# Revit family: LAMP_HANCE 48V 1000-2000 SPOT DALI
name_source: partatom
category: Luminarias
revit_build: Autodesk Revit 2015 (Build: 20140606_1530(x64)
units: mm (PartAtom-declared; Revit-internal decimal feet)

## types (12) — shared parameters
CRI = 80
Comentarios de tipo = Availability of tilting between 0º and 90º, rotation between 0º and 355º and change ring color when placed in a project.
Diameter = 65 mm  [stored 0.213255 ft]
Elevación por defecto = 1219 mm
Fabricante = LAMP
Gear = Adjustable DALI
Height = 135 mm  [stored 0.442913 ft]
IEE = A+
Installation instructions = https://www.lamp.es
Insulation class = III
Lamp = COB LED
Last update = 02/04/2019
Luminaire type = Indoor - Spotlight
MacAdam = 3
Manufacturer URL = http://www.lamp.es
Manufacturer country = Spain
Manufacturer name = LAMP
Model explanation = Availability of tilting between 0º and 90º, rotation between 0º and 355º and change ring color when placed in a project.
Power Supply = 48V DC
Product URL = https://www.lamp.es
Product datasheet = http://www.lamp.es
Protection rating = IP20
Type = COB PHILIPS
Weight = 0.44 kg

## per-type parameters (varying)
| type | Descripción | Efficacy | Finish | Initial color | Initial intensity | LED Lifetime | Material tija | Modelo | Photometric web file | Plum | Power | Product code |
| 657LM 2700 SPOT BLACK | HANCE TRACK 48 1000 VWW SP DALI BK. | 70 lm/W | RAL9011 textured | 2700 K | 657 lm | 50.000 L90 B10 | LAMP_Aluminio Hance Negro | HS1TL10SP827DBB | Cuerpo Hance 48V BASE 1000_2000 (tilting)_SP : 657LM 2700 SPOT BLACK | 9 W | 9 W | HS1TL10SP827DBB |
| 657LM 2700 SPOT WHITE | HANCE TRACK 48 1000 VWW SP DALI WH. | 70 lm/W | RAL9010 textured | 2700 K | 657 lm | 50.000 L90 B10 | LAMP_Aluminio Hance Blanco | HS1TL10SP827DBW | Cuerpo Hance 48V BASE 1000_2000 (tilting)_SP : 657LM 2700 SPOT WHITE | 9 W | 9 W | HS1TL10SP827DBW |
| 670LM 3000 SPOT BLACK | HANCE TRACK 48 1000 WW SP DALI BK. | 71 lm/W | RAL9011 textured | 3000 K | 670 lm | 50.000 L90 B10 | LAMP_Aluminio Hance Negro | HS1TL10SP830DBB | Cuerpo Hance 48V BASE 1000_2000 (tilting)_SP : 670LM 3000 SPOT BLACK | 9 W | 9 W | HS1TL10SP830DBB |
| 670LM 3000 SPOT WHITE | HANCE TRACK 48 1000 WW SP DALI WH. | 71 lm/W | RAL9010 textured | 3000 K | 670 lm | 50.000 L90 B10 | LAMP_Aluminio Hance Negro | HS1TL10SP830DBW | Cuerpo Hance 48V BASE 1000_2000 (tilting)_SP : 670LM 3000 SPOT WHITE | 9 W | 9 W | HS1TL10SP830DBW |
| 710LM 4000 SPOT BLACK | HANCE TRACK 48 1000 NW SP DALI BK. | 76 lm/W | RAL9011 textured | 4000 K | 710 lm | 50.000 L90 B10 | LAMP_Aluminio Hance Negro | HS1TL10SP840DBB | Cuerpo Hance 48V BASE 1000_2000 (tilting)_SP : 710LM 4000 SPOT BLACK | 9 W | 9 W | HS1TL10SP840DBB |
| 710LM 4000 SPOT WHITE | HANCE TRACK 48 1000 NW SP DALI WH. | 76 lm/W | RAL9010 textured | 4000 K | 710 lm | 50.000 L90 B10 | LAMP_Aluminio Hance Blanco | HS1TL10SP840DBW | Cuerpo Hance 48V BASE 1000_2000 (tilting)_SP : 710LM 4000 SPOT WHITE | 9 W | 9 W | HS1TL10SP840DBW |
| 1427LM 2700 SPOT BLACK | HANCE TRACK 48 2000 VWW SP DALI BK. | 84 lm/W | RAL9011 textured | 2700 K | 1427 lm | 50.000 L80 B10 | LAMP_Aluminio Hance Negro | HS1TL20SP827DBB | Cuerpo Hance 48V BASE 1000_2000 (tilting)_SP : 1427LM 2700 SPOT BLACK | 17 W | 18 W | HS1TL20SP827DBB |
| 1427LM 2700 SPOT WHITE | HANCE TRACK 48 2000 VWW SP DALI WH. | 84 lm/W | RAL9010 textured | 2700 K | 1427 lm | 50.000 L80 B10 | LAMP_Aluminio Hance Blanco | HS1TL20SP827DBW | Cuerpo Hance 48V BASE 1000_2000 (tilting)_SP : 1427LM 2700 SPOT WHITE | 17 W | 18 W | HS1TL20SP827DBW |
| 1456LM 3000 SPOT BLACK | HANCE TRACK 48 2000 WW SP DALI BK. | 86 lm/W | RAL9011 textured | 3000 K | 1456 lm | 50.000 L80 B10 | LAMP_Aluminio Hance Negro | HS1TL20SP830DBB | Cuerpo Hance 48V BASE 1000_2000 (tilting)_SP : 1456LM 3000 SPOT BLACK | 17 W | 18 W | HS1TL20SP830DBB |
| 1456LM 3000 SPOT WHITE | HANCE TRACK 48 2000 WW SP DALI WH. | 86 lm/W | RAL9010 textured | 3000 K | 1456 lm | 50.000 L80 B10 | LAMP_Aluminio Hance Blanco | HS1TL20SP830DBW | Cuerpo Hance 48V BASE 1000_2000 (tilting)_SP : 1456LM 3000 SPOT WHITE | 17 W | 18 W | HS1TL20SP830DBW |
| 1542LM 4000 SPOT BLACK | HANCE TRACK 48 2000 NW SP DALI BK. | 91 lm/W | RAL9011 textured | 4000 K | 1542 lm | 50.000 L80 B10 | LAMP_Aluminio Hance Negro | HS1TL20SP840DBB | Cuerpo Hance 48V BASE 1000_2000 (tilting)_SP : 1542LM 4000 SPOT BLACK | 17 W | 18 W | HS1TL20SP840DBB |
| 1542LM 4000 SPOT WHITE | HANCE TRACK 48 2000 NW SP DALI WH. | 91 lm/W | RAL9010 textured | 4000 K | 1542 lm | 50.000 L80 B10 | LAMP_Aluminio Hance Blanco | HS1TL20SP840DBW | Cuerpo Hance 48V BASE 1000_2000 (tilting)_SP : 1542LM 4000 SPOT WHITE | 17 W | 18 W | HS1TL20SP840DBW |

note: [stored X ft] marks values corroborated as IEEE doubles in the binary element streams (Revit-internal decimal feet)
